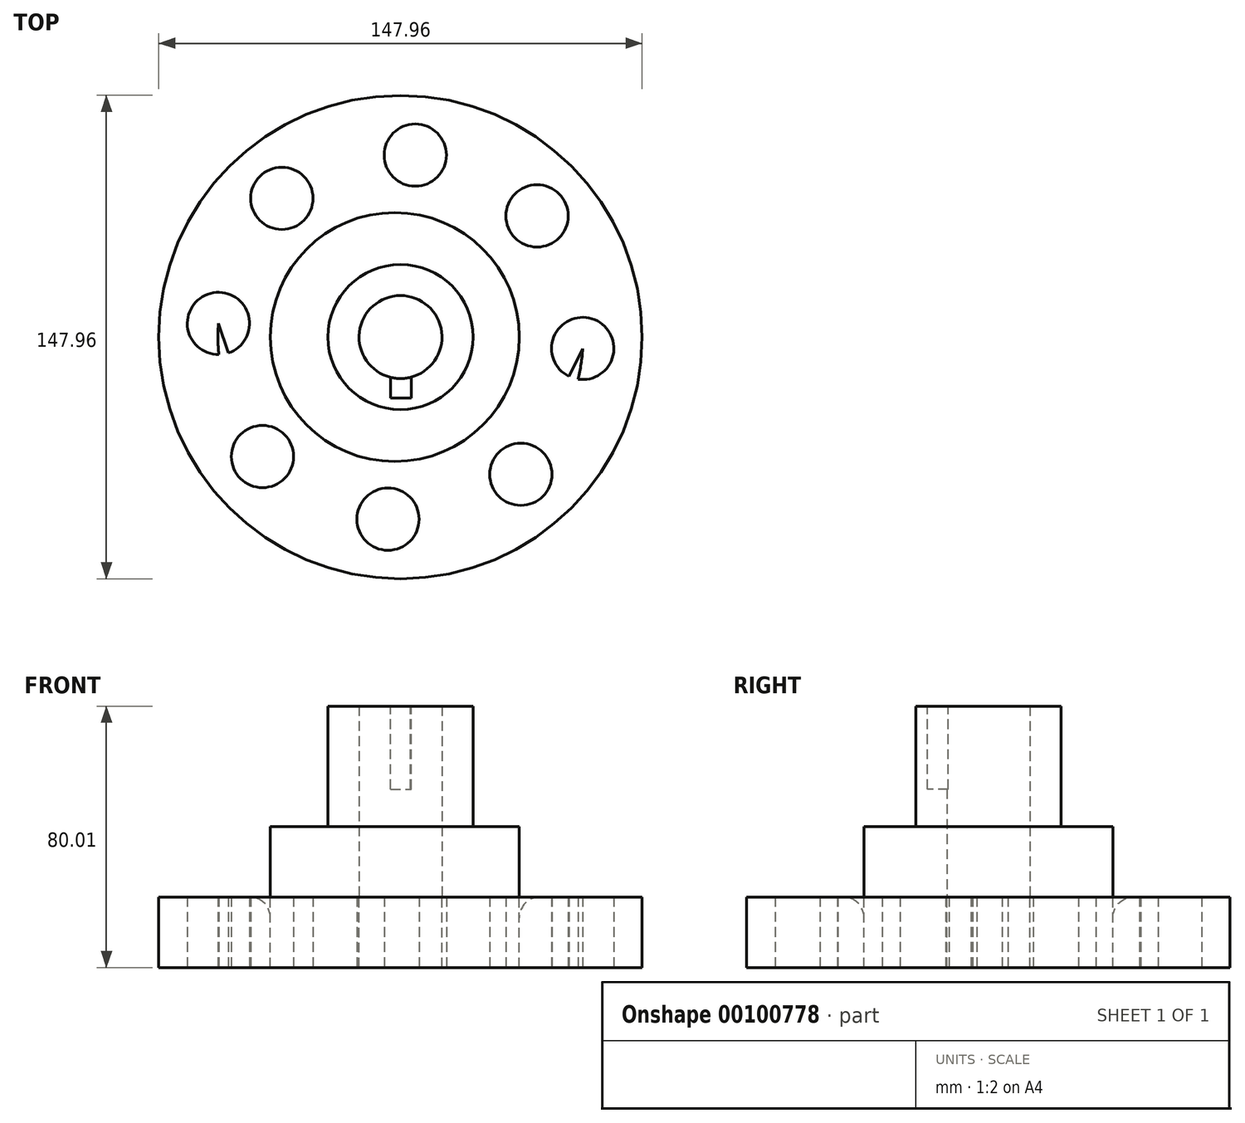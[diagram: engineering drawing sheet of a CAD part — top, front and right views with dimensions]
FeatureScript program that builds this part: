
annotation { "Feature Type Name" : "Feature", "Feature Type Description" : "" }
export const myFeature = defineFeature(function(context is Context, id is Id, definition is map)
    precondition{}
    {
        {
            var Q0;
            Q0=qCreatedBy(makeId("Top.planeOp"),FACE);
            var sketch = newSketch(context, id + "F0", { "sketchPlane" : qUnion([Q0])});
            skCircle(sketch, "E0", {"center": v(0, 0) * mm, "radius": 12.7 * mm});
            skCircle(sketch, "E1", {"center": v(0, 0) * mm, "radius": 22.23 * mm});
            skSolve(sketch);
        }
        {
            var Q0;
            Q0=makeQuery(id+"F0.imprint","IMPRINT",FACE,{"disambiguationData":[TD([[makeQuery(id+"F0.imprint","IMPRINT",EDGE,{"derivedFrom":sQuery(id+"F0.wireOp",EDGE,"E0")}),-1.0]])]});
            extrude(context, id + "F1", {"entities" : qUnion([Q0]), "depth" : 58.42 * mm});
        }
        {
            var Q0;
            Q0=qCreatedBy(makeId("Top.planeOp"),FACE);
            var sketch = newSketch(context, id + "F2", { "sketchPlane" : qUnion([Q0])});
            skCircle(sketch, "E2", {"center": v(-1.75, 0) * mm, "radius": 38.1 * mm});
            skCircle(sketch, "E3", {"center": v(0, 0) * mm, "radius": 55.88 * mm});
            skCircle(sketch, "E4", {"center": v(0, 0) * mm, "radius": 73.98 * mm});
            skSolve(sketch);
        }
        {
            var Q0;
            Q0=makeQuery(id+"F2.imprint","IMPRINT",FACE,{"disambiguationData":[TD([[makeQuery(id+"F2.imprint","IMPRINT",EDGE,{"derivedFrom":sQuery(id+"F2.wireOp",EDGE,"E2")}),1.0]])]});
            extrude(context, id + "F3", {"entities" : qUnion([Q0]), "operationType" : NewBodyOperationType.ADD, "depth" : 21.59 * mm});
        }
        {
            var Q0;
            Q0=makeQuery(id+"F3.boolean.opBoolean","SPLIT",FACE,{"disambiguationData":[TD([makeQuery(id+"F1.opExtrude","SWEPT_FACE",FACE,{"disambiguationData":[OSD([sQuery(id+"F0.wireOp",EDGE,"E0")])]})])],"derivedFrom":makeQuery(id+"F3.opExtrude","CAP_FACE",FACE,{"disambiguationData":[OSD([sQuery(id+"F2.wireOp",EDGE,"E2")])],"isStart":false})});
            extrude(context, id + "F4", {"entities" : qUnion([Q0]), "operationType" : NewBodyOperationType.REMOVE, "endBound" : BoundingType.THROUGH_ALL, "oppositeDirection" : true, "depth" : 25.4 * mm});
        }
        {
            var Q0;
            Q0=makeQuery(id+"F2.imprint","IMPRINT",FACE,{"disambiguationData":[TD([[makeQuery(id+"F2.imprint","IMPRINT",EDGE,{"derivedFrom":sQuery(id+"F2.wireOp",EDGE,"E2")}),-1.0]])]});
            extrude(context, id + "F5", {"entities" : qUnion([Q0]), "oppositeDirection" : true, "depth" : 21.59 * mm});
        }
        {
            var Q0;
            Q0=makeQuery(id+"F2.imprint","IMPRINT",FACE,{"disambiguationData":[TD([[makeQuery(id+"F2.imprint","IMPRINT",EDGE,{"derivedFrom":sQuery(id+"F2.wireOp",EDGE,"E3")}),-1.0]])]});
            extrude(context, id + "F6", {"entities" : qUnion([Q0]), "operationType" : NewBodyOperationType.ADD, "oppositeDirection" : true, "depth" : 21.59 * mm});
        }
        {
            var Q0;
            Q0=makeQuery(id+"F2.imprint","IMPRINT",FACE,{"disambiguationData":[TD([[makeQuery(id+"F2.imprint","IMPRINT",EDGE,{"derivedFrom":sQuery(id+"F2.wireOp",EDGE,"E2")}),1.0]])]});
            extrude(context, id + "F7", {"entities" : qUnion([Q0]), "oppositeDirection" : true, "depth" : 21.59 * mm});
        }
        {
            var Q0;
            Q0=qCreatedBy(makeId("Top.planeOp"),FACE);
            var sketch = newSketch(context, id + "F8", { "sketchPlane" : qUnion([Q0])});
            skCircle(sketch, "E5", {"center": v(0, 0) * mm, "radius": 12.7 * mm});
            skSolve(sketch);
        }
        {
            var Q0;
            Q0 = qSketchRegion(id + "F8", true);
            extrude(context, id + "F9", {"entities" : qUnion([Q0]), "operationType" : NewBodyOperationType.REMOVE, "endBound" : BoundingType.THROUGH_ALL, "oppositeDirection" : true, "depth" : 25.4 * mm});
        }
        {
            var Q0;
            Q0=makeQuery(id+"F1.opExtrude","CAP_FACE",FACE,{"disambiguationData":[OSD([sQuery(id+"F0.wireOp",EDGE,"E0"),sQuery(id+"F0.wireOp",EDGE,"E1")])],"isStart":false});
            var sketch = newSketch(context, id + "F10", { "sketchPlane" : qUnion([Q0])});
            skLineSegment(sketch, "E6.bottom", {"start": v(7.1, 74.94) * mm, "end": v(13.45, 74.94) * mm});
            skLineSegment(sketch, "E6.top", {"start": v(7.1, 68.59) * mm, "end": v(13.45, 68.59) * mm});
            skLineSegment(sketch, "E6.left", {"start": v(7.1, 74.94) * mm, "end": v(7.1, 68.59) * mm});
            skLineSegment(sketch, "E6.right", {"start": v(13.45, 74.94) * mm, "end": v(13.45, 68.59) * mm});
            skLineSegment(sketch, "E7.bottom", {"start": v(-3.04, -12.33) * mm, "end": v(3.3, -12.33) * mm});
            skLineSegment(sketch, "E7.top", {"start": v(-3.04, -18.68) * mm, "end": v(3.3, -18.68) * mm});
            skLineSegment(sketch, "E7.left", {"start": v(-3.04, -12.33) * mm, "end": v(-3.04, -18.68) * mm});
            skLineSegment(sketch, "E7.right", {"start": v(3.3, -12.33) * mm, "end": v(3.3, -18.68) * mm});
            skSolve(sketch);
        }
        {
            var Q0;
            Q0=makeQuery(id+"F10.imprint","IMPRINT",FACE,{"disambiguationData":[TD([[makeQuery(id+"F10.imprint","IMPRINT",EDGE,{"derivedFrom":sQuery(id+"F10.wireOp",EDGE,"E7.top")}),1.0]])]});
            extrude(context, id + "F11", {"entities" : qUnion([Q0]), "operationType" : NewBodyOperationType.REMOVE, "oppositeDirection" : true, "depth" : 25.4 * mm});
        }
        {
            var Q0;
            {var subQ0=sQuery(id+"F2.wireOp",EDGE,"E3");Q0=makeQuery(id+"F6.boolean.opBoolean","MERGE",FACE,{"derivedFrom":[makeQuery(id+"F5.opExtrude","CAP_FACE",FACE,{"disambiguationData":[OSD([sQuery(id+"F2.wireOp",EDGE,"E2"),subQ0])],"isStart":false}),makeQuery(id+"F6.opExtrude","CAP_FACE",FACE,{"disambiguationData":[OSD([subQ0,sQuery(id+"F2.wireOp",EDGE,"E4")])],"isStart":false})]});}
            var sketch = newSketch(context, id + "F12", { "sketchPlane" : qUnion([Q0])});
            skCircle(sketch, "E8", {"center": v(0, 0) * mm, "radius": 55.88 * mm});
            skCircle(sketch, "E9", {"center": v(-42.24, 36.58) * mm, "radius": 9.53 * mm});
            skCircle(sketch, "E10", {"center": v(-3.83, 55.75) * mm, "radius": 9.53 * mm});
            skCircle(sketch, "E11", {"center": v(36.84, 42.02) * mm, "radius": 9.53 * mm});
            skCircle(sketch, "E12", {"center": v(41.8, -37.1) * mm, "radius": 9.53 * mm});
            skCircle(sketch, "E13", {"center": v(4.51, -55.7) * mm, "radius": 9.53 * mm});
            skCircle(sketch, "E14", {"center": v(-36.32, -42.47) * mm, "radius": 9.53 * mm});
            skCircle(sketch, "E15", {"center": v(-55.72, -4.17) * mm, "radius": 9.53 * mm});
            skCircle(sketch, "E16", {"center": v(55.77, 3.5) * mm, "radius": 9.53 * mm});
            skLineSegment(sketch, "E17", {"start": v(55.77, 3.5) * mm, "end": v(41.8, -37.1) * mm});
            skLineSegment(sketch, "E18", {"start": v(36.84, 42.02) * mm, "end": v(55.77, 3.5) * mm});
            skLineSegment(sketch, "E19", {"start": v(-3.83, 55.75) * mm, "end": v(36.84, 42.02) * mm});
            skLineSegment(sketch, "E20", {"start": v(-42.24, 36.58) * mm, "end": v(-3.83, 55.75) * mm});
            skLineSegment(sketch, "E21", {"start": v(-42.24, 36.58) * mm, "end": v(-55.72, -4.17) * mm});
            skLineSegment(sketch, "E22", {"start": v(-55.72, -4.17) * mm, "end": v(-36.32, -42.47) * mm});
            skLineSegment(sketch, "E23", {"start": v(-36.32, -42.47) * mm, "end": v(4.51, -55.7) * mm});
            skLineSegment(sketch, "E24", {"start": v(41.8, -37.1) * mm, "end": v(4.51, -55.7) * mm});
            skSolve(sketch);
        }
        {
            var Q0;
            {var subQ0=sQuery(id+"F12.wireOp",EDGE,"E8");var subQ2=sQuery(id+"F12.wireOp",EDGE,"E12");var subQ3=makeQuery(id+"F12.imprint","INTERSECT",VERTEX,{"disambiguationData":[OD(0.0)],"derivedFrom":[subQ0,subQ2]});Q0=makeQuery(id+"F12.imprint","IMPRINT",FACE,{"disambiguationData":[TD([[makeQuery(id+"F12.imprint","IMPRINT",EDGE,{"disambiguationData":[TD([[subQ3,-1.0]])],"derivedFrom":subQ2}),1.0]])]});}
            var Q1;
            {var subQ1=sQuery(id+"F12.wireOp",EDGE,"E8");var subQ3=sQuery(id+"F12.wireOp",EDGE,"E12");var subQ4=makeQuery(id+"F12.imprint","INTERSECT",VERTEX,{"disambiguationData":[OD(0.0)],"derivedFrom":[subQ1,subQ3]});Q1=makeQuery(id+"F12.imprint","IMPRINT",FACE,{"disambiguationData":[TD([[makeQuery(id+"F12.imprint","IMPRINT",EDGE,{"disambiguationData":[TD([[subQ4,1.0]])],"derivedFrom":subQ3}),1.0]])]});}
            var Q2;
            {var subQ0=sQuery(id+"F12.wireOp",EDGE,"E17");var subQ1=sQuery(id+"F12.wireOp",EDGE,"E12");var subQ2=makeQuery(id+"F12.imprint","INTERSECT",VERTEX,{"derivedFrom":[subQ1,subQ0]});Q2=makeQuery(id+"F12.imprint","IMPRINT",FACE,{"disambiguationData":[TD([[makeQuery(id+"F12.imprint","IMPRINT",EDGE,{"disambiguationData":[TD([[subQ2,-1.0]])],"derivedFrom":subQ1}),1.0]])]});}
            var Q3;
            {var subQ1=sQuery(id+"F12.wireOp",EDGE,"E8");var subQ3=sQuery(id+"F12.wireOp",EDGE,"E12");var subQ4=makeQuery(id+"F12.imprint","INTERSECT",VERTEX,{"disambiguationData":[OD(1.0)],"derivedFrom":[subQ1,subQ3]});Q3=makeQuery(id+"F12.imprint","IMPRINT",FACE,{"disambiguationData":[TD([[makeQuery(id+"F12.imprint","IMPRINT",EDGE,{"disambiguationData":[TD([[subQ4,-1.0]])],"derivedFrom":subQ3}),1.0]])]});}
            extrude(context, id + "F13", {"entities" : qUnion([Q0, Q1, Q2, Q3]), "operationType" : NewBodyOperationType.REMOVE, "endBound" : BoundingType.THROUGH_ALL, "oppositeDirection" : true, "depth" : 25.4 * mm});
        }
        {
            var Q0;
            {var subQ0=sQuery(id+"F12.wireOp",EDGE,"E18");var subQ1=sQuery(id+"F12.wireOp",EDGE,"E16");var subQ2=makeQuery(id+"F12.imprint","INTERSECT",VERTEX,{"derivedFrom":[subQ1,subQ0]});Q0=makeQuery(id+"F12.imprint","IMPRINT",FACE,{"disambiguationData":[TD([[makeQuery(id+"F12.imprint","IMPRINT",EDGE,{"disambiguationData":[TD([[subQ2,-1.0]])],"derivedFrom":subQ1}),1.0]])]});}
            var Q1;
            {var subQ0=sQuery(id+"F12.wireOp",EDGE,"E8");var subQ2=sQuery(id+"F12.wireOp",EDGE,"E16");var subQ3=makeQuery(id+"F12.imprint","INTERSECT",VERTEX,{"disambiguationData":[OD(0.0)],"derivedFrom":[subQ0,subQ2]});Q1=makeQuery(id+"F12.imprint","IMPRINT",FACE,{"disambiguationData":[TD([[makeQuery(id+"F12.imprint","IMPRINT",EDGE,{"disambiguationData":[TD([[subQ3,1.0]])],"derivedFrom":subQ2}),1.0]])]});}
            var Q2;
            {var subQ1=sQuery(id+"F12.wireOp",EDGE,"E8");var subQ3=sQuery(id+"F12.wireOp",EDGE,"E16");var subQ4=makeQuery(id+"F12.imprint","INTERSECT",VERTEX,{"disambiguationData":[OD(1.0)],"derivedFrom":[subQ1,subQ3]});Q2=makeQuery(id+"F12.imprint","IMPRINT",FACE,{"disambiguationData":[TD([[makeQuery(id+"F12.imprint","IMPRINT",EDGE,{"disambiguationData":[TD([[subQ4,1.0]])],"derivedFrom":subQ3}),1.0]])]});}
            var Q3;
            {var subQ1=sQuery(id+"F12.wireOp",EDGE,"E8");var subQ3=sQuery(id+"F12.wireOp",EDGE,"E16");var subQ4=makeQuery(id+"F12.imprint","INTERSECT",VERTEX,{"disambiguationData":[OD(0.0)],"derivedFrom":[subQ1,subQ3]});Q3=makeQuery(id+"F12.imprint","IMPRINT",FACE,{"disambiguationData":[TD([[makeQuery(id+"F12.imprint","IMPRINT",EDGE,{"disambiguationData":[TD([[subQ4,-1.0]])],"derivedFrom":subQ3}),1.0]])]});}
            extrude(context, id + "F14", {"entities" : qUnion([Q0, Q1, Q2, Q3]), "operationType" : NewBodyOperationType.REMOVE, "endBound" : BoundingType.THROUGH_ALL, "oppositeDirection" : true, "depth" : 25.4 * mm});
        }
        {
            var Q0;
            {var subQ0=sQuery(id+"F12.wireOp",EDGE,"E19");var subQ1=sQuery(id+"F12.wireOp",EDGE,"E11");var subQ2=makeQuery(id+"F12.imprint","INTERSECT",VERTEX,{"derivedFrom":[subQ1,subQ0]});Q0=makeQuery(id+"F12.imprint","IMPRINT",FACE,{"disambiguationData":[TD([[makeQuery(id+"F12.imprint","IMPRINT",EDGE,{"disambiguationData":[TD([[subQ2,-1.0]])],"derivedFrom":subQ1}),1.0]])]});}
            var Q1;
            {var subQ1=sQuery(id+"F12.wireOp",EDGE,"E8");var subQ3=sQuery(id+"F12.wireOp",EDGE,"E11");var subQ4=makeQuery(id+"F12.imprint","INTERSECT",VERTEX,{"disambiguationData":[OD(0.0)],"derivedFrom":[subQ1,subQ3]});Q1=makeQuery(id+"F12.imprint","IMPRINT",FACE,{"disambiguationData":[TD([[makeQuery(id+"F12.imprint","IMPRINT",EDGE,{"disambiguationData":[TD([[subQ4,1.0]])],"derivedFrom":subQ3}),1.0]])]});}
            var Q2;
            {var subQ0=sQuery(id+"F12.wireOp",EDGE,"E8");var subQ2=sQuery(id+"F12.wireOp",EDGE,"E11");var subQ3=makeQuery(id+"F12.imprint","INTERSECT",VERTEX,{"disambiguationData":[OD(0.0)],"derivedFrom":[subQ0,subQ2]});Q2=makeQuery(id+"F12.imprint","IMPRINT",FACE,{"disambiguationData":[TD([[makeQuery(id+"F12.imprint","IMPRINT",EDGE,{"disambiguationData":[TD([[subQ3,-1.0]])],"derivedFrom":subQ2}),1.0]])]});}
            var Q3;
            {var subQ1=sQuery(id+"F12.wireOp",EDGE,"E8");var subQ3=sQuery(id+"F12.wireOp",EDGE,"E11");var subQ4=makeQuery(id+"F12.imprint","INTERSECT",VERTEX,{"disambiguationData":[OD(1.0)],"derivedFrom":[subQ1,subQ3]});Q3=makeQuery(id+"F12.imprint","IMPRINT",FACE,{"disambiguationData":[TD([[makeQuery(id+"F12.imprint","IMPRINT",EDGE,{"disambiguationData":[TD([[subQ4,-1.0]])],"derivedFrom":subQ3}),1.0]])]});}
            extrude(context, id + "F15", {"entities" : qUnion([Q0, Q1, Q2, Q3]), "operationType" : NewBodyOperationType.REMOVE, "endBound" : BoundingType.THROUGH_ALL, "oppositeDirection" : true, "depth" : 25.4 * mm});
        }
        {
            var Q0;
            {var subQ0=sQuery(id+"F12.wireOp",EDGE,"E20");var subQ1=sQuery(id+"F12.wireOp",EDGE,"E10");var subQ2=makeQuery(id+"F12.imprint","INTERSECT",VERTEX,{"derivedFrom":[subQ1,subQ0]});Q0=makeQuery(id+"F12.imprint","IMPRINT",FACE,{"disambiguationData":[TD([[makeQuery(id+"F12.imprint","IMPRINT",EDGE,{"disambiguationData":[TD([[subQ2,-1.0]])],"derivedFrom":subQ1}),1.0]])]});}
            var Q1;
            {var subQ0=sQuery(id+"F12.wireOp",EDGE,"E8");var subQ2=sQuery(id+"F12.wireOp",EDGE,"E10");var subQ3=makeQuery(id+"F12.imprint","INTERSECT",VERTEX,{"disambiguationData":[OD(0.0)],"derivedFrom":[subQ0,subQ2]});Q1=makeQuery(id+"F12.imprint","IMPRINT",FACE,{"disambiguationData":[TD([[makeQuery(id+"F12.imprint","IMPRINT",EDGE,{"disambiguationData":[TD([[subQ3,-1.0]])],"derivedFrom":subQ2}),1.0]])]});}
            var Q2;
            {var subQ0=sQuery(id+"F12.wireOp",EDGE,"E8");var subQ2=sQuery(id+"F12.wireOp",EDGE,"E9");var subQ3=makeQuery(id+"F12.imprint","INTERSECT",VERTEX,{"disambiguationData":[OD(0.0)],"derivedFrom":[subQ0,subQ2]});Q2=makeQuery(id+"F12.imprint","IMPRINT",FACE,{"disambiguationData":[TD([[makeQuery(id+"F12.imprint","IMPRINT",EDGE,{"disambiguationData":[TD([[subQ3,-1.0]])],"derivedFrom":subQ2}),1.0]])]});}
            var Q3;
            {var subQ0=sQuery(id+"F12.wireOp",EDGE,"E20");var subQ1=sQuery(id+"F12.wireOp",EDGE,"E9");var subQ2=makeQuery(id+"F12.imprint","INTERSECT",VERTEX,{"derivedFrom":[subQ1,subQ0]});Q3=makeQuery(id+"F12.imprint","IMPRINT",FACE,{"disambiguationData":[TD([[makeQuery(id+"F12.imprint","IMPRINT",EDGE,{"disambiguationData":[TD([[subQ2,1.0]])],"derivedFrom":subQ1}),1.0]])]});}
            var Q4;
            {var subQ1=sQuery(id+"F12.wireOp",EDGE,"E8");var subQ3=sQuery(id+"F12.wireOp",EDGE,"E9");var subQ4=makeQuery(id+"F12.imprint","INTERSECT",VERTEX,{"disambiguationData":[OD(1.0)],"derivedFrom":[subQ1,subQ3]});Q4=makeQuery(id+"F12.imprint","IMPRINT",FACE,{"disambiguationData":[TD([[makeQuery(id+"F12.imprint","IMPRINT",EDGE,{"disambiguationData":[TD([[subQ4,-1.0]])],"derivedFrom":subQ3}),1.0]])]});}
            var Q5;
            {var subQ1=sQuery(id+"F12.wireOp",EDGE,"E8");var subQ3=sQuery(id+"F12.wireOp",EDGE,"E10");var subQ4=makeQuery(id+"F12.imprint","INTERSECT",VERTEX,{"disambiguationData":[OD(0.0)],"derivedFrom":[subQ1,subQ3]});Q5=makeQuery(id+"F12.imprint","IMPRINT",FACE,{"disambiguationData":[TD([[makeQuery(id+"F12.imprint","IMPRINT",EDGE,{"disambiguationData":[TD([[subQ4,1.0]])],"derivedFrom":subQ3}),1.0]])]});}
            var Q6;
            {var subQ1=sQuery(id+"F12.wireOp",EDGE,"E8");var subQ3=sQuery(id+"F12.wireOp",EDGE,"E10");var subQ4=makeQuery(id+"F12.imprint","INTERSECT",VERTEX,{"disambiguationData":[OD(1.0)],"derivedFrom":[subQ1,subQ3]});Q6=makeQuery(id+"F12.imprint","IMPRINT",FACE,{"disambiguationData":[TD([[makeQuery(id+"F12.imprint","IMPRINT",EDGE,{"disambiguationData":[TD([[subQ4,-1.0]])],"derivedFrom":subQ3}),1.0]])]});}
            var Q7;
            {var subQ1=sQuery(id+"F12.wireOp",EDGE,"E8");var subQ3=sQuery(id+"F12.wireOp",EDGE,"E9");var subQ4=makeQuery(id+"F12.imprint","INTERSECT",VERTEX,{"disambiguationData":[OD(0.0)],"derivedFrom":[subQ1,subQ3]});Q7=makeQuery(id+"F12.imprint","IMPRINT",FACE,{"disambiguationData":[TD([[makeQuery(id+"F12.imprint","IMPRINT",EDGE,{"disambiguationData":[TD([[subQ4,1.0]])],"derivedFrom":subQ3}),1.0]])]});}
            extrude(context, id + "F16", {"entities" : qUnion([Q0, Q1, Q2, Q3, Q4, Q5, Q6, Q7]), "operationType" : NewBodyOperationType.REMOVE, "endBound" : BoundingType.THROUGH_ALL, "oppositeDirection" : true, "depth" : 25.4 * mm});
        }
        {
            var Q0;
            {var subQ0=sQuery(id+"F12.wireOp",EDGE,"E8");var subQ2=sQuery(id+"F12.wireOp",EDGE,"E13");var subQ3=makeQuery(id+"F12.imprint","INTERSECT",VERTEX,{"disambiguationData":[OD(0.0)],"derivedFrom":[subQ0,subQ2]});Q0=makeQuery(id+"F12.imprint","IMPRINT",FACE,{"disambiguationData":[TD([[makeQuery(id+"F12.imprint","IMPRINT",EDGE,{"disambiguationData":[TD([[subQ3,-1.0]])],"derivedFrom":subQ2}),1.0]])]});}
            var Q1;
            {var subQ1=sQuery(id+"F12.wireOp",EDGE,"E8");var subQ3=sQuery(id+"F12.wireOp",EDGE,"E13");var subQ4=makeQuery(id+"F12.imprint","INTERSECT",VERTEX,{"disambiguationData":[OD(1.0)],"derivedFrom":[subQ1,subQ3]});Q1=makeQuery(id+"F12.imprint","IMPRINT",FACE,{"disambiguationData":[TD([[makeQuery(id+"F12.imprint","IMPRINT",EDGE,{"disambiguationData":[TD([[subQ4,-1.0]])],"derivedFrom":subQ3}),1.0]])]});}
            var Q2;
            {var subQ0=sQuery(id+"F12.wireOp",EDGE,"E24");var subQ1=sQuery(id+"F12.wireOp",EDGE,"E13");var subQ2=makeQuery(id+"F12.imprint","INTERSECT",VERTEX,{"derivedFrom":[subQ1,subQ0]});Q2=makeQuery(id+"F12.imprint","IMPRINT",FACE,{"disambiguationData":[TD([[makeQuery(id+"F12.imprint","IMPRINT",EDGE,{"disambiguationData":[TD([[subQ2,-1.0]])],"derivedFrom":subQ1}),1.0]])]});}
            var Q3;
            {var subQ1=sQuery(id+"F12.wireOp",EDGE,"E8");var subQ3=sQuery(id+"F12.wireOp",EDGE,"E13");var subQ4=makeQuery(id+"F12.imprint","INTERSECT",VERTEX,{"disambiguationData":[OD(0.0)],"derivedFrom":[subQ1,subQ3]});Q3=makeQuery(id+"F12.imprint","IMPRINT",FACE,{"disambiguationData":[TD([[makeQuery(id+"F12.imprint","IMPRINT",EDGE,{"disambiguationData":[TD([[subQ4,1.0]])],"derivedFrom":subQ3}),1.0]])]});}
            extrude(context, id + "F17", {"entities" : qUnion([Q0, Q1, Q2, Q3]), "operationType" : NewBodyOperationType.REMOVE, "endBound" : BoundingType.THROUGH_ALL, "oppositeDirection" : true, "depth" : 25.4 * mm});
        }
        {
            var Q0;
            {var subQ0=sQuery(id+"F12.wireOp",EDGE,"E8");var subQ2=sQuery(id+"F12.wireOp",EDGE,"E14");var subQ3=makeQuery(id+"F12.imprint","INTERSECT",VERTEX,{"disambiguationData":[OD(0.0)],"derivedFrom":[subQ0,subQ2]});Q0=makeQuery(id+"F12.imprint","IMPRINT",FACE,{"disambiguationData":[TD([[makeQuery(id+"F12.imprint","IMPRINT",EDGE,{"disambiguationData":[TD([[subQ3,-1.0]])],"derivedFrom":subQ2}),1.0]])]});}
            var Q1;
            {var subQ0=sQuery(id+"F12.wireOp",EDGE,"E22");var subQ1=sQuery(id+"F12.wireOp",EDGE,"E14");var subQ2=makeQuery(id+"F12.imprint","INTERSECT",VERTEX,{"derivedFrom":[subQ1,subQ0]});Q1=makeQuery(id+"F12.imprint","IMPRINT",FACE,{"disambiguationData":[TD([[makeQuery(id+"F12.imprint","IMPRINT",EDGE,{"disambiguationData":[TD([[subQ2,1.0]])],"derivedFrom":subQ1}),1.0]])]});}
            var Q2;
            {var subQ1=sQuery(id+"F12.wireOp",EDGE,"E8");var subQ3=sQuery(id+"F12.wireOp",EDGE,"E14");var subQ4=makeQuery(id+"F12.imprint","INTERSECT",VERTEX,{"disambiguationData":[OD(0.0)],"derivedFrom":[subQ1,subQ3]});Q2=makeQuery(id+"F12.imprint","IMPRINT",FACE,{"disambiguationData":[TD([[makeQuery(id+"F12.imprint","IMPRINT",EDGE,{"disambiguationData":[TD([[subQ4,1.0]])],"derivedFrom":subQ3}),1.0]])]});}
            var Q3;
            {var subQ1=sQuery(id+"F12.wireOp",EDGE,"E8");var subQ3=sQuery(id+"F12.wireOp",EDGE,"E14");var subQ4=makeQuery(id+"F12.imprint","INTERSECT",VERTEX,{"disambiguationData":[OD(1.0)],"derivedFrom":[subQ1,subQ3]});Q3=makeQuery(id+"F12.imprint","IMPRINT",FACE,{"disambiguationData":[TD([[makeQuery(id+"F12.imprint","IMPRINT",EDGE,{"disambiguationData":[TD([[subQ4,-1.0]])],"derivedFrom":subQ3}),1.0]])]});}
            extrude(context, id + "F18", {"entities" : qUnion([Q0, Q1, Q2, Q3]), "operationType" : NewBodyOperationType.REMOVE, "endBound" : BoundingType.THROUGH_ALL, "oppositeDirection" : true, "depth" : 25.4 * mm});
        }
        {
            var Q0;
            {var subQ0=sQuery(id+"F12.wireOp",EDGE,"E21");var subQ1=sQuery(id+"F12.wireOp",EDGE,"E15");var subQ2=makeQuery(id+"F12.imprint","INTERSECT",VERTEX,{"derivedFrom":[subQ1,subQ0]});Q0=makeQuery(id+"F12.imprint","IMPRINT",FACE,{"disambiguationData":[TD([[makeQuery(id+"F12.imprint","IMPRINT",EDGE,{"disambiguationData":[TD([[subQ2,1.0]])],"derivedFrom":subQ1}),1.0]])]});}
            var Q1;
            {var subQ0=sQuery(id+"F12.wireOp",EDGE,"E8");var subQ2=sQuery(id+"F12.wireOp",EDGE,"E15");var subQ3=makeQuery(id+"F12.imprint","INTERSECT",VERTEX,{"disambiguationData":[OD(0.0)],"derivedFrom":[subQ0,subQ2]});Q1=makeQuery(id+"F12.imprint","IMPRINT",FACE,{"disambiguationData":[TD([[makeQuery(id+"F12.imprint","IMPRINT",EDGE,{"disambiguationData":[TD([[subQ3,-1.0]])],"derivedFrom":subQ2}),1.0]])]});}
            var Q2;
            {var subQ1=sQuery(id+"F12.wireOp",EDGE,"E8");var subQ3=sQuery(id+"F12.wireOp",EDGE,"E15");var subQ4=makeQuery(id+"F12.imprint","INTERSECT",VERTEX,{"disambiguationData":[OD(1.0)],"derivedFrom":[subQ1,subQ3]});Q2=makeQuery(id+"F12.imprint","IMPRINT",FACE,{"disambiguationData":[TD([[makeQuery(id+"F12.imprint","IMPRINT",EDGE,{"disambiguationData":[TD([[subQ4,-1.0]])],"derivedFrom":subQ3}),1.0]])]});}
            var Q3;
            {var subQ1=sQuery(id+"F12.wireOp",EDGE,"E8");var subQ3=sQuery(id+"F12.wireOp",EDGE,"E15");var subQ4=makeQuery(id+"F12.imprint","INTERSECT",VERTEX,{"disambiguationData":[OD(0.0)],"derivedFrom":[subQ1,subQ3]});Q3=makeQuery(id+"F12.imprint","IMPRINT",FACE,{"disambiguationData":[TD([[makeQuery(id+"F12.imprint","IMPRINT",EDGE,{"disambiguationData":[TD([[subQ4,1.0]])],"derivedFrom":subQ3}),1.0]])]});}
            extrude(context, id + "F19", {"entities" : qUnion([Q0, Q1, Q2, Q3]), "operationType" : NewBodyOperationType.REMOVE, "endBound" : BoundingType.THROUGH_ALL, "oppositeDirection" : true, "depth" : 25.4 * mm});
        }
        {
            var Q0;
            Q0=makeQuery(id+"F5.opExtrude","CAP_EDGE",EDGE,{"disambiguationData":[OSD([sQuery(id+"F2.wireOp",EDGE,"E2")])],"isStart":true});
            fillet(context, id + "F20", {"entities" : qUnion([Q0]), "radius" : 6.35 * mm, "tangentPropagation" : true, "allowEdgeOverflow" : false});
        }
    });
